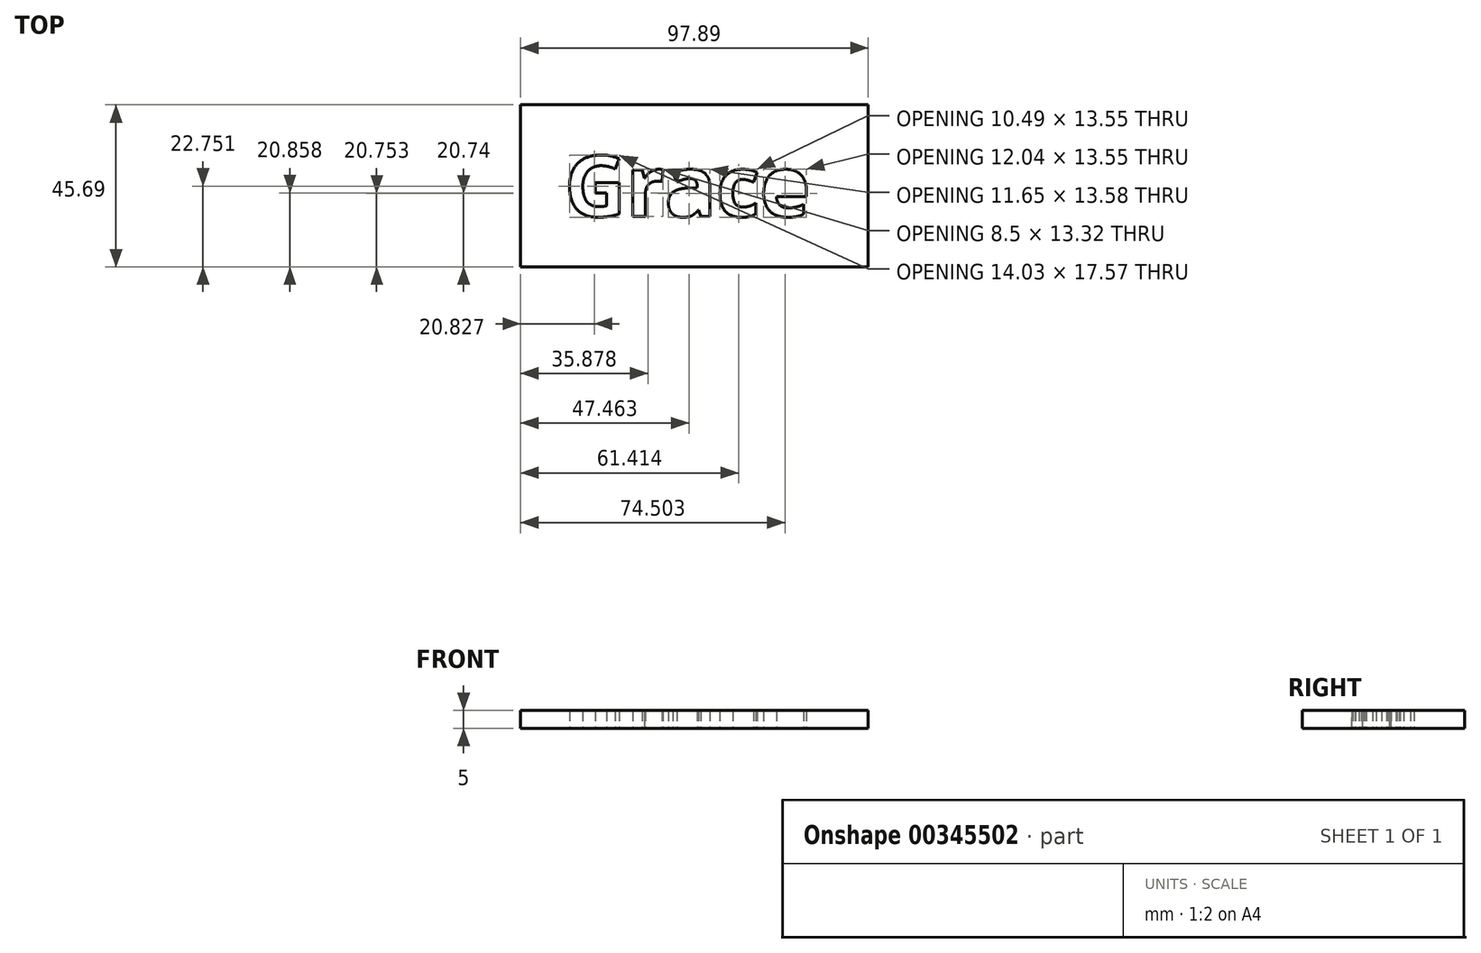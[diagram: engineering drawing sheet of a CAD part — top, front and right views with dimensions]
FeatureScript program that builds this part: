
annotation { "Feature Type Name" : "Feature", "Feature Type Description" : "" }
export const myFeature = defineFeature(function(context is Context, id is Id, definition is map)
    precondition{}
    {
        {
            var Q0;
            Q0=qCreatedBy(makeId("Top.planeOp"),FACE);
            var sketch = newSketch(context, id + "F0", { "sketchPlane" : qUnion([Q0])});
            skLineSegment(sketch, "E0.bottom", {"start": v(-47.72, -31.44) * mm, "end": v(50.17, -31.44) * mm});
            skLineSegment(sketch, "E0.top", {"start": v(-47.72, 14.25) * mm, "end": v(50.17, 14.25) * mm});
            skLineSegment(sketch, "E0.left", {"start": v(-47.72, -31.44) * mm, "end": v(-47.72, 14.25) * mm});
            skLineSegment(sketch, "E0.right", {"start": v(50.17, -31.44) * mm, "end": v(50.17, 14.25) * mm});
            skText(sketch, "E1", { "text": "Grace", "fontName": "OpenSans-Bold.ttf"});
            const initialGuessF0  = {"E1": [-0.0353, -0.01724, 1, 0, 0.01724]};
            skSetInitialGuess(sketch, initialGuessF0);
            skSolve(sketch);
        }
        {
            var Q0;
            Q0 = qSketchRegion(id + "F0", true);
            extrude(context, id + "F1", {"entities" : qUnion([Q0]), "depth" : 5 * mm});
        }
    });
